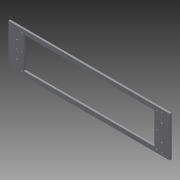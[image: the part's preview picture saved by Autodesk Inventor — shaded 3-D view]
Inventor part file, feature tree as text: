
AUTODESK INVENTOR PART (.ipt)
format: ipt  version: 2014 SP1 (Build 180222100, 222)  size: 125,440 bytes
history: native  units: mm
features: extrude x1, sketch x1
ambient origin geometry x8: Origin, YZ Plane, XZ Plane, XY Plane, X Axis, Y Axis, Z Axis, Center Point
bodies: Solid1 (feature_tree)
feature tree (2):
  extrude  "Extrusion1"  [1 undecoded]
  sketch  "Sketch1"  dims[d0=4.0mm d1=0.0mm]
note: 1 required parameter value undecoded (feature->parameter linkage not recoverable at this tier; creation-order binding heuristic only, values carry confidence <= 0.55)
